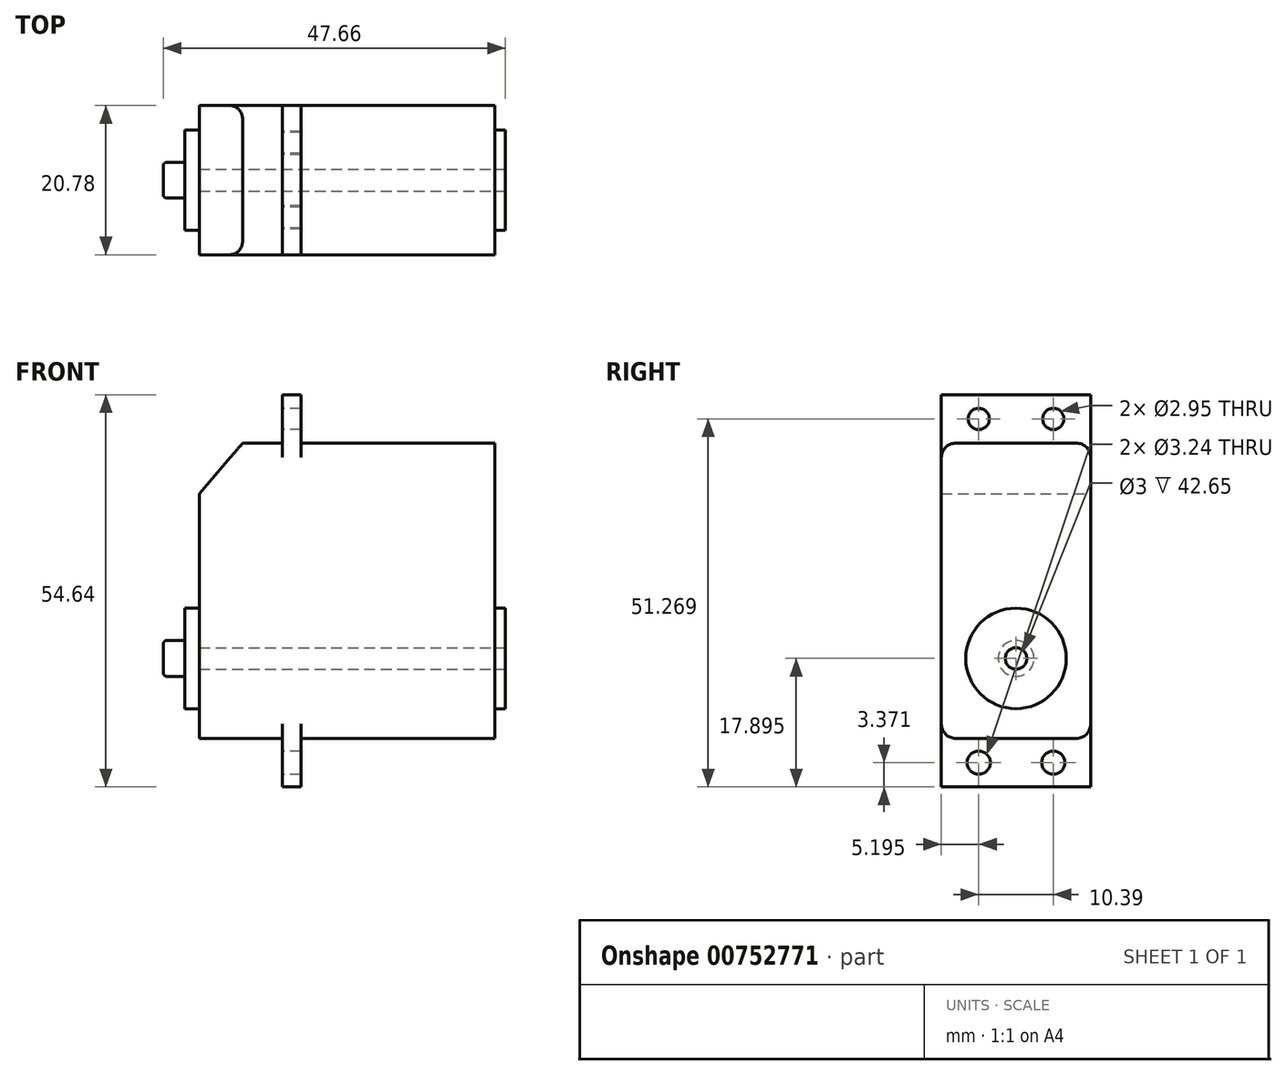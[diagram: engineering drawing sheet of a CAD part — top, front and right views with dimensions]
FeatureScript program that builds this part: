
annotation { "Feature Type Name" : "Feature", "Feature Type Description" : "" }
export const myFeature = defineFeature(function(context is Context, id is Id, definition is map)
    precondition{}
    {
        {
            var Q0;
            Q0=qCreatedBy(makeId("Front.planeOp"),FACE);
            var sketch = newSketch(context, id + "F0", { "sketchPlane" : qUnion([Q0])});
            skLineSegment(sketch, "E0.bottom", {"start": v(20.58, -20.57) * mm, "end": v(-6.4, -20.57) * mm});
            skLineSegment(sketch, "E0.top", {"start": v(20.57, 20.58) * mm, "end": v(-6.4, 20.58) * mm});
            skLineSegment(sketch, "E0.left", {"start": v(20.58, -20.57) * mm, "end": v(20.57, 20.58) * mm});
            skLineSegment(sketch, "E0.right", {"start": v(-20.57, -20.58) * mm, "end": v(-20.58, 13.53) * mm});
            skPoint(sketch, "E0.middle", {"position": v(0, 0) * mm});
            skLineSegment(sketch, "E1", {"start": v(-20.58, 13.53) * mm, "end": v(-14.52, 20.57) * mm});
            skLineSegment(sketch, "E2", {"start": v(20.58, 0) * mm, "end": v(-7.69, 0) * mm});
            skLineSegment(sketch, "E3.bottom", {"start": v(-6.4, -27.32) * mm, "end": v(-8.97, -27.32) * mm});
            skLineSegment(sketch, "E3.top", {"start": v(-6.4, 27.32) * mm, "end": v(-8.97, 27.32) * mm});
            skLineSegment(sketch, "E3.left", {"start": v(-6.4, -27.32) * mm, "end": v(-6.4, -20.58) * mm});
            skLineSegment(sketch, "E3.right", {"start": v(-8.97, -27.32) * mm, "end": v(-8.97, -20.57) * mm});
            skPoint(sketch, "E3.middle", {"position": v(-7.69, 0) * mm});
            skLineSegment(sketch, "E4.trimOffspring", {"start": v(-8.97, 20.58) * mm, "end": v(-14.53, 20.57) * mm});
            skLineSegment(sketch, "E5.trimOffspring", {"start": v(-8.97, -20.57) * mm, "end": v(-20.57, -20.58) * mm});
            skLineSegment(sketch, "E6.trimOffspring", {"start": v(-8.97, 20.57) * mm, "end": v(-8.97, 27.32) * mm});
            skLineSegment(sketch, "E7.trimOffspring", {"start": v(-6.4, 20.57) * mm, "end": v(-6.4, 27.32) * mm});
            skSolve(sketch);
        }
        {
            var Q0;
            Q0 = qSketchRegion(id + "F0", true);
            extrude(context, id + "F1", {"entities" : qUnion([Q0]), "depth" : 20.78 * mm, "offsetDistance" : 25 * mm});
        }
        {
            var Q0;
            Q0=makeQuery(id+"F1.opExtrude","SWEPT_FACE",FACE,{"disambiguationData":[OSD([sQuery(id+"F0.wireOp",EDGE,"E6.trimOffspring")])]});
            var sketch = newSketch(context, id + "F2", { "sketchPlane" : qUnion([Q0])});
            skLineSegment(sketch, "E8", {"start": v(0, 23.95) * mm, "end": v(20.78, 23.95) * mm});
            skLineSegment(sketch, "E9", {"start": v(10.4, 23.95) * mm, "end": v(0, 23.95) * mm});
            skCircle(sketch, "E10", {"center": v(5.2, 23.95) * mm, "radius": 1.48 * mm});
            skLineSegment(sketch, "E11", {"start": v(10.4, 23.95) * mm, "end": v(10.4, 27.32) * mm});
            skCircle(sketch, "E12.MirrorC", {"center": v(15.59, 23.95) * mm, "radius": 1.48 * mm});
            skSolve(sketch);
        }
        {
            var Q0;
            Q0 = qSketchRegion(id + "F2", true);
            extrude(context, id + "F3", {"entities" : qUnion([Q0]), "operationType" : NewBodyOperationType.REMOVE, "oppositeDirection" : true, "depth" : 10 * mm, "offsetDistance" : 25 * mm});
        }
        {
            var Q0;
            Q0=makeQuery(id+"F1.opExtrude","SWEPT_FACE",FACE,{"disambiguationData":[OSD([sQuery(id+"F0.wireOp",EDGE,"E3.right")])]});
            var sketch = newSketch(context, id + "F4", { "sketchPlane" : qUnion([Q0])});
            skLineSegment(sketch, "E13", {"start": v(0, -23.95) * mm, "end": v(20.78, -23.95) * mm});
            skLineSegment(sketch, "E14", {"start": v(20.78, -23.95) * mm, "end": v(10.4, -23.95) * mm});
            skLineSegment(sketch, "E15", {"start": v(10.4, -23.95) * mm, "end": v(10.4, -20.58) * mm});
            skCircle(sketch, "E16", {"center": v(15.59, -23.95) * mm, "radius": 1.62 * mm});
            skCircle(sketch, "E17.MirrorC", {"center": v(5.2, -23.95) * mm, "radius": 1.62 * mm});
            skSolve(sketch);
        }
        {
            var Q0;
            Q0 = qSketchRegion(id + "F4", true);
            extrude(context, id + "F5", {"entities" : qUnion([Q0]), "operationType" : NewBodyOperationType.REMOVE, "oppositeDirection" : true, "depth" : 25 * mm, "offsetDistance" : 25 * mm});
        }
        {
            var Q0;
            Q0=makeQuery(id+"F1.opExtrude","CAP_EDGE",EDGE,{"disambiguationData":[OSD([sQuery(id+"F0.wireOp",EDGE,"E0.top")])],"isStart":false});
            var Q1;
            Q1=makeQuery(id+"F1.opExtrude","CAP_EDGE",EDGE,{"disambiguationData":[OSD([sQuery(id+"F0.wireOp",EDGE,"E4.trimOffspring")])],"isStart":false});
            var Q2;
            Q2=makeQuery(id+"F1.opExtrude","CAP_EDGE",EDGE,{"disambiguationData":[OSD([sQuery(id+"F0.wireOp",EDGE,"E4.trimOffspring")])],"isStart":true});
            var Q3;
            Q3=makeQuery(id+"F1.opExtrude","CAP_EDGE",EDGE,{"disambiguationData":[OSD([sQuery(id+"F0.wireOp",EDGE,"E0.top")])],"isStart":true});
            var Q4;
            Q4=makeQuery(id+"F1.opExtrude","CAP_EDGE",EDGE,{"disambiguationData":[OSD([sQuery(id+"F0.wireOp",EDGE,"E0.bottom")])],"isStart":false});
            var Q5;
            Q5=makeQuery(id+"F1.opExtrude","CAP_EDGE",EDGE,{"disambiguationData":[OSD([sQuery(id+"F0.wireOp",EDGE,"E5.trimOffspring")])],"isStart":false});
            var Q6;
            Q6=makeQuery(id+"F1.opExtrude","CAP_EDGE",EDGE,{"disambiguationData":[OSD([sQuery(id+"F0.wireOp",EDGE,"E0.bottom")])],"isStart":true});
            var Q7;
            Q7=makeQuery(id+"F1.opExtrude","CAP_EDGE",EDGE,{"disambiguationData":[OSD([sQuery(id+"F0.wireOp",EDGE,"E5.trimOffspring")])],"isStart":true});
            fillet(context, id + "F6", {"entities" : qUnion([Q0, Q1, Q2, Q3, Q4, Q5, Q6, Q7]), "radius" : 2 * mm, "tangentPropagation" : true, "allowEdgeOverflow" : false});
        }
        {
            var Q0;
            Q0=makeQuery(id+"F1.opExtrude","SWEPT_FACE",FACE,{"disambiguationData":[OSD([sQuery(id+"F0.wireOp",EDGE,"E0.left")])]});
            var sketch = newSketch(context, id + "F7", { "sketchPlane" : qUnion([Q0])});
            skLineSegment(sketch, "E18", {"start": v(-10.4, 20.57) * mm, "end": v(-10.4, -9.42) * mm});
            skCircle(sketch, "E19", {"center": v(-10.4, -9.42) * mm, "radius": 7 * mm});
            skSolve(sketch);
        }
        {
            var Q0;
            Q0 = qSketchRegion(id + "F7", true);
            extrude(context, id + "F8", {"entities" : qUnion([Q0]), "operationType" : NewBodyOperationType.ADD, "depth" : 1.5 * mm, "offsetDistance" : 25 * mm});
        }
        {
            var Q0;
            Q0=makeQuery(id+"F8.opExtrude","CAP_FACE",FACE,{"disambiguationData":[OSD([sQuery(id+"F7.wireOp",EDGE,"E19")])],"isStart":false});
            var sketch = newSketch(context, id + "F9", { "sketchPlane" : qUnion([Q0])});
            skCircle(sketch, "E20", {"center": v(-10.4, -9.42) * mm, "radius": 1.5 * mm});
            skSolve(sketch);
        }
        {
            var Q0;
            Q0 = qSketchRegion(id + "F9", true);
            extrude(context, id + "F10", {"entities" : qUnion([Q0]), "operationType" : NewBodyOperationType.REMOVE, "oppositeDirection" : true, "depth" : 50 * mm, "offsetDistance" : 25 * mm});
        }
        {
            var Q0;
            Q0=makeQuery(id+"F1.opExtrude","SWEPT_FACE",FACE,{"disambiguationData":[OSD([sQuery(id+"F0.wireOp",EDGE,"E0.right")])]});
            var sketch = newSketch(context, id + "F11", { "sketchPlane" : qUnion([Q0])});
            skCircle(sketch, "E21", {"center": v(10.4, -9.42) * mm, "radius": 7 * mm});
            skSolve(sketch);
        }
        {
            var Q0;
            Q0 = qSketchRegion(id + "F11", true);
            extrude(context, id + "F12", {"entities" : qUnion([Q0]), "operationType" : NewBodyOperationType.ADD, "depth" : 2 * mm, "offsetDistance" : 25 * mm});
        }
        {
            var Q0;
            Q0=makeQuery(id+"F12.opExtrude","CAP_FACE",FACE,{"disambiguationData":[OSD([sQuery(id+"F11.wireOp",EDGE,"E21")])],"isStart":false});
            var sketch = newSketch(context, id + "F13", { "sketchPlane" : qUnion([Q0])});
            skCircle(sketch, "E22", {"center": v(10.4, -9.42) * mm, "radius": 2.5 * mm});
            skSolve(sketch);
        }
        {
            var Q0;
            Q0=makeQuery(id+"F13.imprint","IMPRINT",FACE,{"disambiguationData":[TD([[makeQuery(id+"F13.imprint","IMPRINT",EDGE,{"derivedFrom":sQuery(id+"F13.wireOp",EDGE,"E22")}),1.0]])]});
            extrude(context, id + "F14", {"entities" : qUnion([Q0]), "operationType" : NewBodyOperationType.ADD, "depth" : 3 * mm, "offsetDistance" : 25 * mm});
        }
        {
            var Q0;
            Q0=makeQuery(id+"F14.opExtrude","CAP_EDGE",EDGE,{"disambiguationData":[OSD([sQuery(id+"F13.wireOp",EDGE,"E22")])],"isStart":false});
            fillet(context, id + "F15", {"entities" : qUnion([Q0]), "radius" : 0.5 * mm, "tangentPropagation" : true, "allowEdgeOverflow" : false});
        }
    });
